# Revit family: Tomas sin enclavamiento  20_25 V
name_source: partatom
category: Installations électriques
revit_build: Autodesk Revit 2018 (Build: 20170223_1515(x64)
units: mm (PartAtom-declared; Revit-internal decimal feet)

## family parameters
Conserver l'orientation des annotations = Non
Cote de connecteur circulaire = Utiliser le diamètre
Couper avec des vides une fois chargée = Non
Hôte = Face
Partagée = Non
Point de calcul de pièce = Non
Type d'élément = Normal

## types (2) — shared parameters
Elévation par défaut = 1000 mm  [stored 3.28084 ft]
Estándar CEI o NFC = CEI
Fabricant = Legrand
Familia produce = 0854-P17 TEMPRA PRO
Temperatura maxima de uso = 40
Temperatura minima de uso = -25
Tension V = 20 25 V  50/60 Hz purpura
Toma estándar internacional para montaje empotrado o montaje en superficie con accesorio permite la conexión de dispositivos de alimentación = Toma estándar internacional para montaje empotrado o montaje en superficie con accesorio permite la conexión de dispositivos de alimentación
altura mm = 84 mm
ancho mm = 84 mm
clase de protección IP = IP44
color característico = purpura
distancia de fijación horizontal mm = 70 mm
distancia de fijación vertical mm = 70 mm
instalación de empotrar E o de superficie S = empotrar y superficie
materia de la caja = plástico
numero de polos = 2
profundidad de empotrar mm = 33 mm  [stored 0.108268 ft]
profundidad mm = 66 mm
resistencia a los choques IK = 9
sin halogeno = Oui
tipo de conexión = conexión por tonillo
zero-valued in all types: posición de la tierra h

## per-type parameters (varying)
| type | Description | intensidad A |
| P17 - IP44 - 32A - 2P | LG-055295_Montaje en panel toma P17 - IP 44 - 20/25 V - 32 A - 2P | 32 A |
| P17 - IP44 - 16 A - 2P | LG-055245_ P17 - IP 44 - 20/25 V - 16 A - 2P | 16 A |

note: [stored X ft] marks values corroborated as IEEE doubles in the binary element streams (Revit-internal decimal feet)
